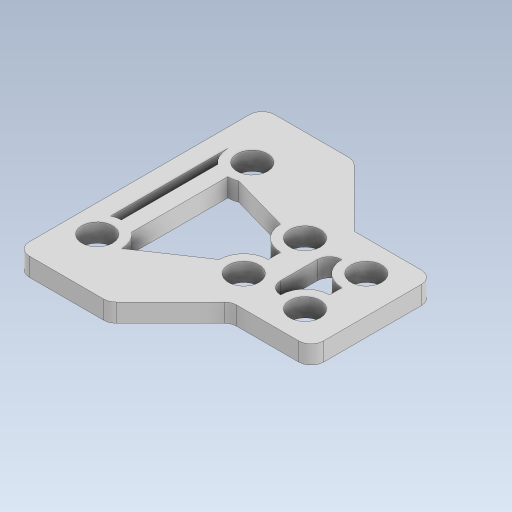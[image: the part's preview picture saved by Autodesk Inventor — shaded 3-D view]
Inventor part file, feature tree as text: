
AUTODESK INVENTOR PART (.ipt)
format: ipt  version: 2023.5 (Build 275446000, 446)  size: 396,800 bytes
history: native  units: mm
features: extrude x1, fillet x1, sketch x1
ambient origin geometry x8: Origin, YZ Plane, XZ Plane, XY Plane, X Axis, Y Axis, Z Axis, Center Point
bodies: Solid1 (feature_tree)
feature tree (3):
  extrude  "Extrusion1"  Depth=40.0mm
  fillet  "Fillet1"  Radius=5.0mm
  sketch  "Sketch1"  dims[d2=36.0mm d3=40.0mm d4=5.0mm d6=5.0mm d8=10.0mm d9=45.0deg d10=3.0mm d11=0.0mm d13=8.0mm d14=2.0mm d15=8.0mm d16=8.0mm d17=13.0mm d18=5.0mm d19=10.0mm d20=8.0mm d22=5.0mm d23=4.5mm d24=8.0mm]
